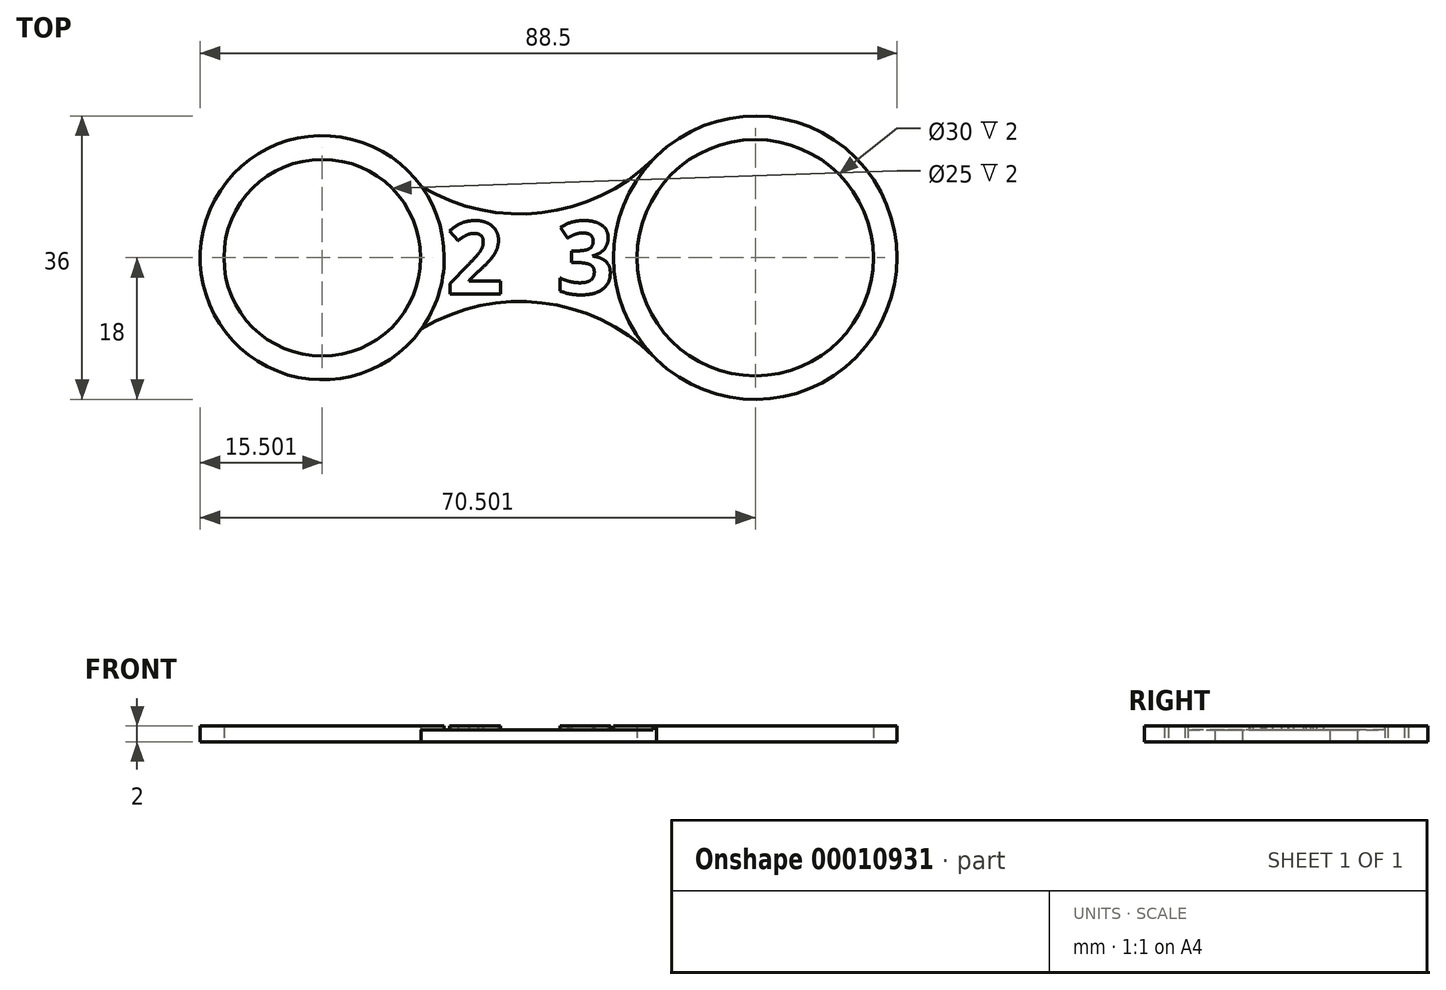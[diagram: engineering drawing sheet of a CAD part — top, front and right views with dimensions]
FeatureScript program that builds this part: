
annotation { "Feature Type Name" : "Feature", "Feature Type Description" : "" }
export const myFeature = defineFeature(function(context is Context, id is Id, definition is map)
    precondition{}
    {
        {
            var Q0;
            Q0=qCreatedBy(makeId("Top.planeOp"),FACE);
            var sketch = newSketch(context, id + "F0", { "sketchPlane" : qUnion([Q0])});
            skCircle(sketch, "E0", {"center": v(-30.7, 0) * mm, "radius": 12.5 * mm});
            skCircle(sketch, "E1", {"center": v(24.3, 0) * mm, "radius": 15 * mm});
            skCircle(sketch, "E2", {"center": v(24.3, 0) * mm, "radius": 18 * mm});
            skCircle(sketch, "E3", {"center": v(-30.7, 0) * mm, "radius": 15.5 * mm});
            skArc(sketch, "E4", {"start": v(-18.12, 9.06) * mm, "mid": v(-2.52, 5.76) * mm, "end": v(11.75, 12.9) * mm});
            skArc(sketch, "E5.0.MirrorCS", {"start": v(-18.12, -9.06) * mm, "mid": v(-2.52, -5.76) * mm, "end": v(11.75, -12.9) * mm});
            skSolve(sketch);
        }
        {
            var Q0;
            Q0=makeQuery(id+"F0.imprint","IMPRINT",FACE,{"disambiguationData":[TD([[makeQuery(id+"F0.imprint","IMPRINT",EDGE,{"derivedFrom":sQuery(id+"F0.wireOp",EDGE,"E1")}),-1.0]])]});
            var Q1;
            Q1=makeQuery(id+"F0.imprint","IMPRINT",FACE,{"disambiguationData":[TD([[makeQuery(id+"F0.imprint","IMPRINT",EDGE,{"derivedFrom":sQuery(id+"F0.wireOp",EDGE,"E0")}),-1.0]])]});
            var Q2;
            {var subQ1=sQuery(id+"F0.wireOp",EDGE,"E2");var subQ5=sQuery(id+"F0.wireOp",EDGE,"E4");var subQ6=makeQuery(id+"F0.imprint","INTERSECT",VERTEX,{"disambiguationData":[OD(1.0)],"derivedFrom":[subQ1,subQ5]});Q2=makeQuery(id+"F0.imprint","IMPRINT",FACE,{"disambiguationData":[TD([[makeQuery(id+"F0.imprint","IMPRINT",EDGE,{"disambiguationData":[TD([[subQ6,-1.0]])],"derivedFrom":subQ1}),-1.0]])]});}
            extrude(context, id + "F1", {"entities" : qUnion([Q0, Q1, Q2]), "depth" : 1.5 * mm});
        }
        {
            var Q0;
            Q0=makeQuery(id+"F0.imprint","IMPRINT",FACE,{"disambiguationData":[TD([[makeQuery(id+"F0.imprint","IMPRINT",EDGE,{"derivedFrom":sQuery(id+"F0.wireOp",EDGE,"E1")}),-1.0]])]});
            var Q1;
            Q1=makeQuery(id+"F0.imprint","IMPRINT",FACE,{"disambiguationData":[TD([[makeQuery(id+"F0.imprint","IMPRINT",EDGE,{"derivedFrom":sQuery(id+"F0.wireOp",EDGE,"E0")}),-1.0]])]});
            extrude(context, id + "F2", {"entities" : qUnion([Q0, Q1]), "operationType" : NewBodyOperationType.ADD, "depth" : 2 * mm});
        }
        {
            var Q0;
            Q0=makeQuery(id+"F1.opExtrude","CAP_FACE",FACE,{"disambiguationData":[OSD([sQuery(id+"F0.wireOp",EDGE,"E0"),sQuery(id+"F0.wireOp",EDGE,"E1"),sQuery(id+"F0.wireOp",EDGE,"E2"),sQuery(id+"F0.wireOp",EDGE,"E3"),sQuery(id+"F0.wireOp",EDGE,"E4"),sQuery(id+"F0.wireOp",EDGE,"E5.0.MirrorCS")])],"isStart":false});
            var sketch = newSketch(context, id + "F3", { "sketchPlane" : qUnion([Q0])});
            skText(sketch, "E6", { "text": "2  3", "fontName": "OpenSans-Bold.ttf"});
            const initialGuessF3  = {"E6": [-0.015, -0.0046, 1, 0, 0.00927]};
            skSetInitialGuess(sketch, initialGuessF3);
            skSolve(sketch);
        }
        {
            var Q0;
            Q0=makeQuery(id+"F3.imprint","IMPRINT",FACE,{"disambiguationData":[TD([[makeQuery(id+"F3.imprint","IMPRINT",EDGE,{"derivedFrom":sQuery(id+"F3.wireOp",EDGE,"E6.sketch_text.stroke-24")}),-1.0]])]});
            var Q1;
            Q1=makeQuery(id+"F3.imprint","IMPRINT",FACE,{"disambiguationData":[TD([[makeQuery(id+"F3.imprint","IMPRINT",EDGE,{"derivedFrom":sQuery(id+"F3.wireOp",EDGE,"E6.sketch_text.stroke-0")}),-1.0]])]});
            extrude(context, id + "F4", {"entities" : qUnion([Q0, Q1]), "operationType" : NewBodyOperationType.ADD, "depth" : .5 * mm});
        }
    });
